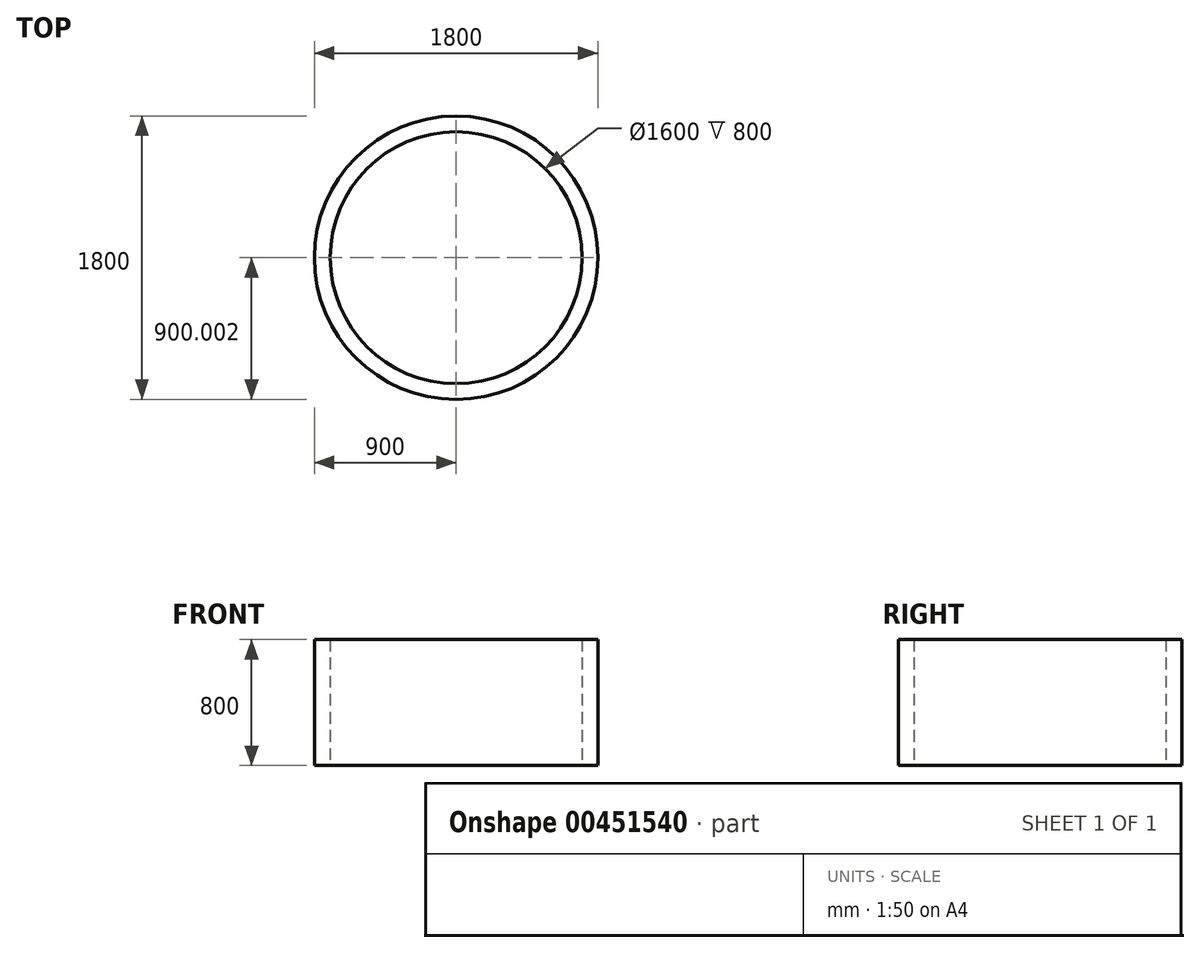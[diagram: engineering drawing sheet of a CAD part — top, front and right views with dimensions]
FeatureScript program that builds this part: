
annotation { "Feature Type Name" : "Feature", "Feature Type Description" : "" }
export const myFeature = defineFeature(function(context is Context, id is Id, definition is map)
    precondition{}
    {
        {
            var Q0;
            Q0=qCreatedBy(makeId("Top.planeOp"),FACE);
            var sketch = newSketch(context, id + "F0", { "sketchPlane" : qUnion([Q0])});
            skCircle(sketch, "E0", {"center": v(0, -1.27) * mm, "radius": 900 * mm});
            skCircle(sketch, "E1", {"center": v(0, -1.27) * mm, "radius": 800 * mm});
            skSolve(sketch);
        }
        {
            var Q0;
            Q0=makeQuery(id+"F0.imprint","IMPRINT",FACE,{"disambiguationData":[TD([[makeQuery(id+"F0.imprint","IMPRINT",EDGE,{"derivedFrom":sQuery(id+"F0.wireOp",EDGE,"E0")}),1.0]])]});
            extrude(context, id + "F1", {"entities" : qUnion([Q0]), "endBound" : BoundingType.SYMMETRIC, "depth" : 800 * mm});
        }
    });
